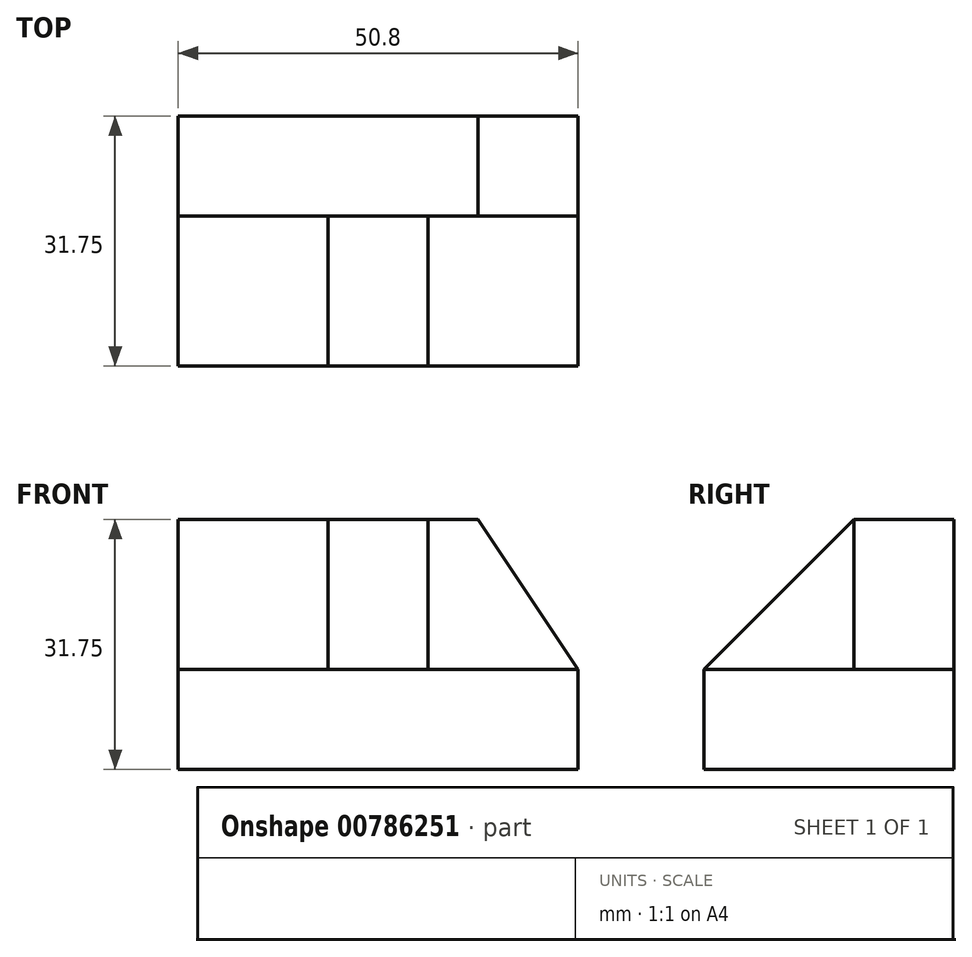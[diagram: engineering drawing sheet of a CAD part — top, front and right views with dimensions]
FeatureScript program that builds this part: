
annotation { "Feature Type Name" : "Feature", "Feature Type Description" : "" }
export const myFeature = defineFeature(function(context is Context, id is Id, definition is map)
    precondition{}
    {
        {
            var Q0;
            Q0=qCreatedBy(makeId("Top.planeOp"),FACE);
            var sketch = newSketch(context, id + "F0", { "sketchPlane" : qUnion([Q0])});
            skLineSegment(sketch, "E0", {"start": v(0, 0) * mm, "end": v(50.8, 0) * mm});
            skLineSegment(sketch, "E1", {"start": v(50.8, 0) * mm, "end": v(50.8, 31.75) * mm});
            skLineSegment(sketch, "E2", {"start": v(50.8, 31.75) * mm, "end": v(0, 31.75) * mm});
            skLineSegment(sketch, "E3", {"start": v(0, 31.75) * mm, "end": v(0, 0) * mm});
            skSolve(sketch);
        }
        {
            var Q0;
            Q0 = qSketchRegion(id + "F0", true);
            extrude(context, id + "F1", {"entities" : qUnion([Q0]), "depth" : 12.7 * mm, "offsetDistance" : 25.4 * mm});
        }
        {
            var Q0;
            Q0=makeQuery(id+"F1.opExtrude","CAP_FACE",FACE,{"disambiguationData":[OSD([sQuery(id+"F0.wireOp",EDGE,"E0"),sQuery(id+"F0.wireOp",EDGE,"E1"),sQuery(id+"F0.wireOp",EDGE,"E2"),sQuery(id+"F0.wireOp",EDGE,"E3")])],"isStart":false});
            var sketch = newSketch(context, id + "F2", { "sketchPlane" : qUnion([Q0])});
            skLineSegment(sketch, "E4", {"start": v(50.8, 31.75) * mm, "end": v(50.8, 19.05) * mm});
            skLineSegment(sketch, "E5", {"start": v(50.8, 19.05) * mm, "end": v(31.75, 19.05) * mm});
            skLineSegment(sketch, "E6", {"start": v(31.75, 19.05) * mm, "end": v(31.75, 0) * mm});
            skLineSegment(sketch, "E7", {"start": v(31.75, 0) * mm, "end": v(19.05, 0) * mm});
            skLineSegment(sketch, "E8", {"start": v(19.05, 0) * mm, "end": v(19.05, 19.05) * mm});
            skLineSegment(sketch, "E9", {"start": v(19.05, 19.05) * mm, "end": v(0, 19.05) * mm});
            skSolve(sketch);
        }
        {
            var Q0;
            Q0=makeQuery(id+"F2.imprint","IMPRINT",FACE,{"disambiguationData":[TD([[makeQuery(id+"F2.imprint","IMPRINT",EDGE,{"derivedFrom":sQuery(id+"F2.wireOp",EDGE,"E4")}),1.0]])]});
            extrude(context, id + "F3", {"entities" : qUnion([Q0]), "operationType" : NewBodyOperationType.ADD, "depth" : 19.05 * mm, "offsetDistance" : 25.4 * mm});
        }
        {
            var Q0;
            Q0=makeQuery(id+"F3.opExtrude","SWEPT_FACE",FACE,{"disambiguationData":[OSD([sQuery(id+"F2.wireOp",EDGE,"E5")])]});
            var sketch = newSketch(context, id + "F4", { "sketchPlane" : qUnion([Q0])});
            skLineSegment(sketch, "E10", {"start": v(50.8, 31.75) * mm, "end": v(38.1, 31.75) * mm});
            skLineSegment(sketch, "E11", {"start": v(38.1, 31.75) * mm, "end": v(50.8, 12.7) * mm});
            skSolve(sketch);
        }
        {
            var Q0;
            Q0=makeQuery(id+"F4.imprint","IMPRINT",FACE,{"disambiguationData":[TD([[makeQuery(id+"F4.imprint","IMPRINT",EDGE,{"derivedFrom":sQuery(id+"F4.wireOp",EDGE,"E10")}),1.0]])]});
            extrude(context, id + "F5", {"entities" : qUnion([Q0]), "operationType" : NewBodyOperationType.REMOVE, "oppositeDirection" : true, "depth" : 12.7 * mm, "offsetDistance" : 25.4 * mm});
        }
        {
            var Q0;
            Q0=makeQuery(id+"F3.opExtrude","SWEPT_FACE",FACE,{"disambiguationData":[OSD([sQuery(id+"F2.wireOp",EDGE,"E6")])]});
            var sketch = newSketch(context, id + "F6", { "sketchPlane" : qUnion([Q0])});
            skLineSegment(sketch, "E12", {"start": v(19.05, 31.75) * mm, "end": v(0, 12.7) * mm});
            skSolve(sketch);
        }
        {
            var Q0;
            Q0=makeQuery(id+"F6.imprint","IMPRINT",FACE,{"disambiguationData":[TD([[makeQuery(id+"F6.imprint","IMPRINT",EDGE,{"derivedFrom":sQuery(id+"F6.wireOp",EDGE,"E12")}),-1.0]])]});
            extrude(context, id + "F7", {"entities" : qUnion([Q0]), "operationType" : NewBodyOperationType.REMOVE, "oppositeDirection" : true, "depth" : 12.7 * mm, "offsetDistance" : 25.4 * mm});
        }
    });
